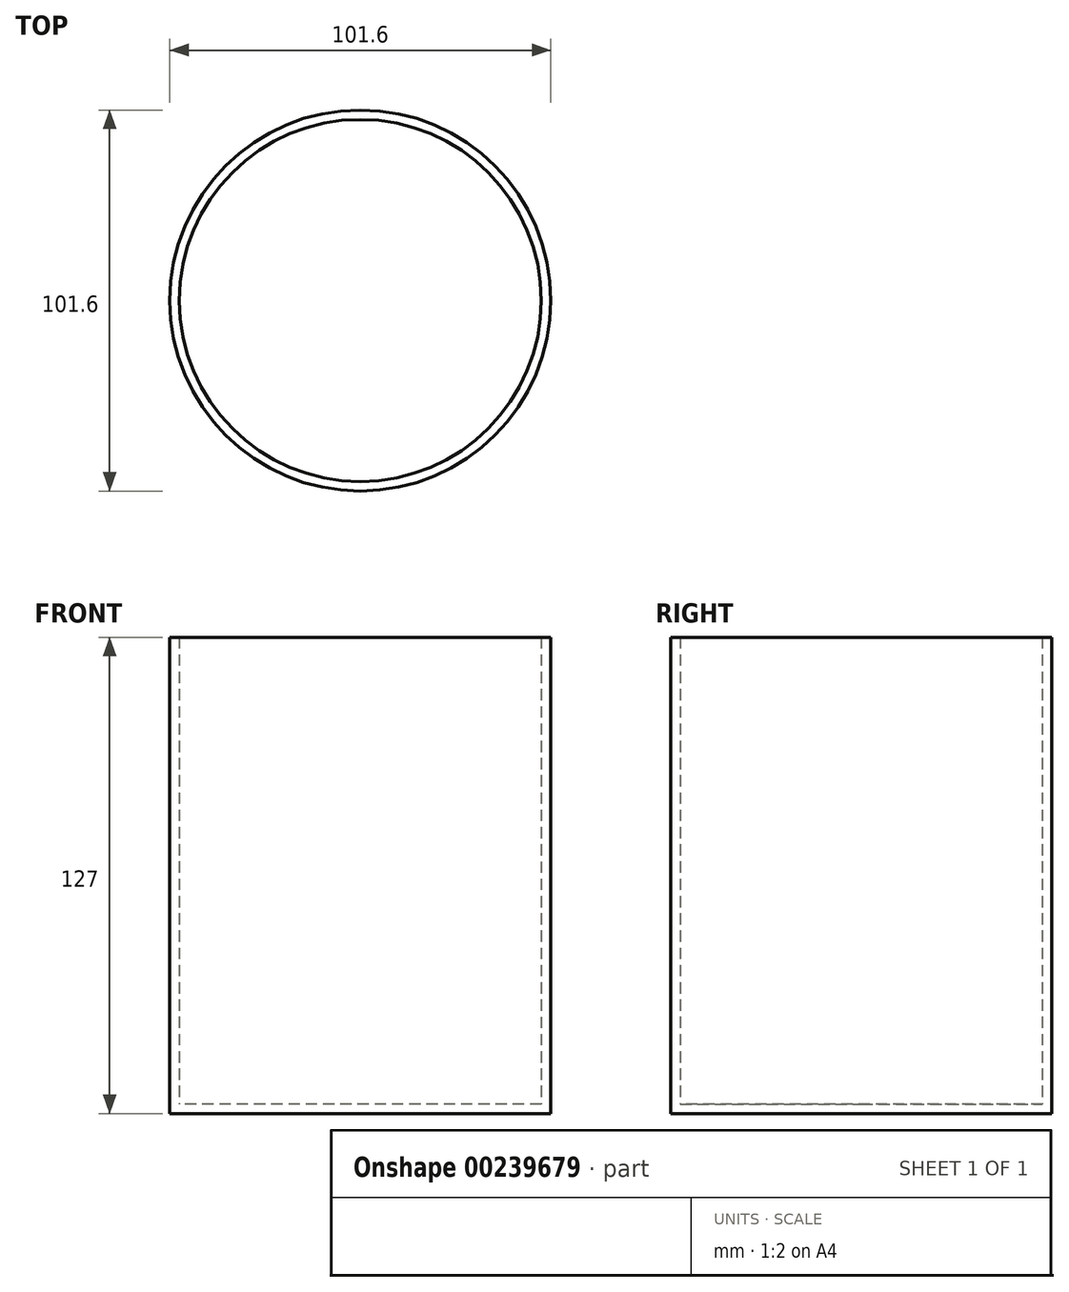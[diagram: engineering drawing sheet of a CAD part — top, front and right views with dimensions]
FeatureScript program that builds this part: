
annotation { "Feature Type Name" : "Feature", "Feature Type Description" : "" }
export const myFeature = defineFeature(function(context is Context, id is Id, definition is map)
    precondition{}
    {
        {
            var Q0;
            Q0=qCreatedBy(makeId("Top.planeOp"),FACE);
            var sketch = newSketch(context, id + "F0", { "sketchPlane" : qUnion([Q0])});
            skCircle(sketch, "E0", {"center": v(0, 0) * mm, "radius": 50.8 * mm});
            skSolve(sketch);
        }
        {
            var Q0;
            Q0 = qSketchRegion(id + "F0", true);
            extrude(context, id + "F1", {"entities" : qUnion([Q0]), "endBound" : BoundingType.SYMMETRIC, "depth" : 127 * mm});
        }
        {
            var Q0;
            Q0=makeQuery(id+"F1.opExtrude","CAP_FACE",FACE,{"disambiguationData":[OSD([sQuery(id+"F0.wireOp",EDGE,"E0")])],"isStart":false});
            shell(context, id + "F2", {"entities" : qUnion([Q0]), "thickness" : 2.54 * mm});
        }
        {
            var Q0;
            Q0=qCreatedBy(makeId("Right.planeOp"),FACE);
            var sketch = newSketch(context, id + "F3", { "sketchPlane" : qUnion([Q0])});
            skFitSpline(sketch, "E1", {"points": [v(-51.07, 40.73) * mm, v(-67.81, 44.24) * mm, v(-51.07, -50.45) * mm], "startDerivative": vector(-68.35, 33.58) * mm, "endDerivative": vector(52.03, -186.14) * mm});
            skSolve(sketch);
        }
        {
            var Q0;
            Q0=sQuery(id+"F3.wireOp",EDGE,"E1");
            extrude(context, id + "F4", {"bodyType" : ToolBodyType.SURFACE, "surfaceEntities" : qUnion([Q0]), "depth" : 16.5 * mm});
        }
    });
